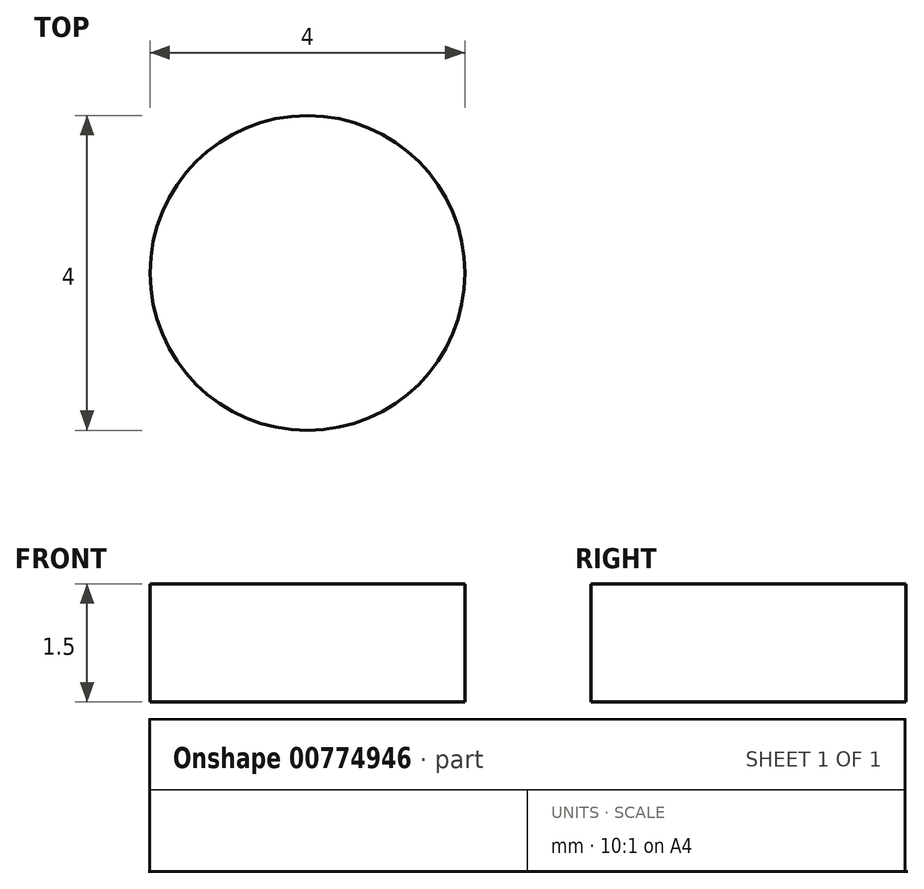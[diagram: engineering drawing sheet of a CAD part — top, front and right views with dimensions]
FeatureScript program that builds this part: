
annotation { "Feature Type Name" : "Feature", "Feature Type Description" : "" }
export const myFeature = defineFeature(function(context is Context, id is Id, definition is map)
    precondition{}
    {
        {
            var Q0;
            Q0=qCreatedBy(makeId("Top.planeOp"),FACE);
            var sketch = newSketch(context, id + "F0", { "sketchPlane" : qUnion([Q0])});
            skCircle(sketch, "E0", {"center": v(0, 0) * mm, "radius": 2 * mm});
            skSolve(sketch);
        }
        {
            var Q0;
            Q0 = qSketchRegion(id + "F0", true);
            extrude(context, id + "F1", {"entities" : qUnion([Q0]), "depth" : 1.5 * mm, "offsetDistance" : 25 * mm});
        }
    });
